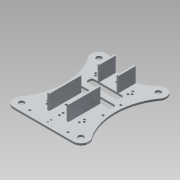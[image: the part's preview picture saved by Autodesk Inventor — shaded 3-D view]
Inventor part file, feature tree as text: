
AUTODESK INVENTOR PART (.ipt)
format: ipt  version: 2015 SP1 (Build 190203100, 203)  size: 392,704 bytes
history: native  units: mm
features: extrude x10, sketch x6, projected_geometry x6, reference x3
ambient origin geometry x8: Origin, YZ Plane, XZ Plane, XY Plane, X Axis, Y Axis, Z Axis, Center Point
bodies: Body1 (feature_tree)
feature tree (25):
  extrude  "Extrusion14"  Depth=3.5mm
  extrude  "Extrusion15"  Depth=3.5mm
  extrude  "Extrusion16"  Depth=5.0mm
  extrude  "Extrusion17"  Depth=2.0mm
  extrude  "Extrusion18"  Depth=23.5mm
  extrude  "Extrusion19"  Depth=23.5mm
  extrude  "Extrusion20"  Depth=23.5mm
  sketch  "Sketch21"  dims[d219=12.747276mm d220=12.747276mm d235=6.458811mm d241=18.458811mm d242=18.458811mm d244=5.0mm]
  extrude  "Extrusion23"  Depth=23.5mm
  extrude  "Extrusion24"  Depth=23.5mm
  extrude  "Extrusion25"  Depth=23.5mm
  sketch  "Sketch1"  dims[d19=46.65mm d72=0.0mm d105=3.5mm]
  sketch  "Sketch14"  dims[d106=3.5mm d198=16.0mm]
  reference  "Reference1"
  reference  "Reference2"
  reference  "Reference3"
  sketch  "Sketch20"  dims[d199=8.65129mm]
  sketch  "Sketch23"  dims[d247=79.203871mm d248=2.0mm]
  projected_geometry  "Projected Loop5"
  projected_geometry  "Projected Loop6"
  projected_geometry  "Projected Loop7"
  projected_geometry  "Projected Loop8"
  sketch  "Sketch24"  dims[d249=3.5mm d250=2.5mm d251=2.5mm d252=146.323246mm d253=146.323245mm d258=6.00224mm d259=27.79742mm d260=69.254481mm d261=3.0mm d262=0.0mm d263=5.821895mm d264=5.821895mm d265=5.821895mm d266=46.987913mm d267=12.022738mm d268=63.629996mm d269=3.0mm d270=0.0mm d271=46.987914mm d272=12.02274mm d275=3.0mm d276=0.0mm d278=3.5mm d279=3.5mm d280=3.0mm d281=0.0mm d285=5.0mm d286=5.0mm d287=3.5mm d288=0.0mm d289=3.5mm d298=3.0mm d299=0.0mm d300=30.0mm d301=5.0mm d302=3.5mm d303=25.0mm d304=9.0mm d305=3.5mm d306=0.0mm d308=1.159189mm d309=16.5mm d310=13.5mm d311=13.5mm d312=16.5mm d317=23.5mm d318=0.0mm d319=47.0mm d320=0.0mm d321=23.5mm d322=0.0mm]
  projected_geometry  "Projected Loop9"
  projected_geometry  "Projected Loop10"
